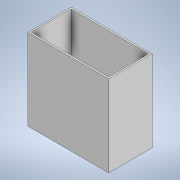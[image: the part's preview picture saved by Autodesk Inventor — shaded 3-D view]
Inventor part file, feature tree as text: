
AUTODESK INVENTOR PART (.ipt)
format: ipt  version: 2020 (Build 240168000, 168)  size: 237,568 bytes
history: native  units: mm
features: extrude x2, sketch x2
ambient origin geometry x8: Origin, YZ Plane, XZ Plane, XY Plane, X Axis, Y Axis, Z Axis, Center Point
bodies: Solid1 (feature_tree)
feature tree (4):
  extrude  "Extrusion1"  Depth=40.0mm
  extrude  "Extrusion2"  Depth=1.5mm
  sketch  "Sketch1"  dims[d0=74.5mm d1=40.0mm]
  sketch  "Sketch2"  dims[d2=75.0mm d3=0.0mm d4=1.5mm d5=1.5mm d6=1.5mm d7=1.5mm d8=73.5mm d9=0.0mm]
